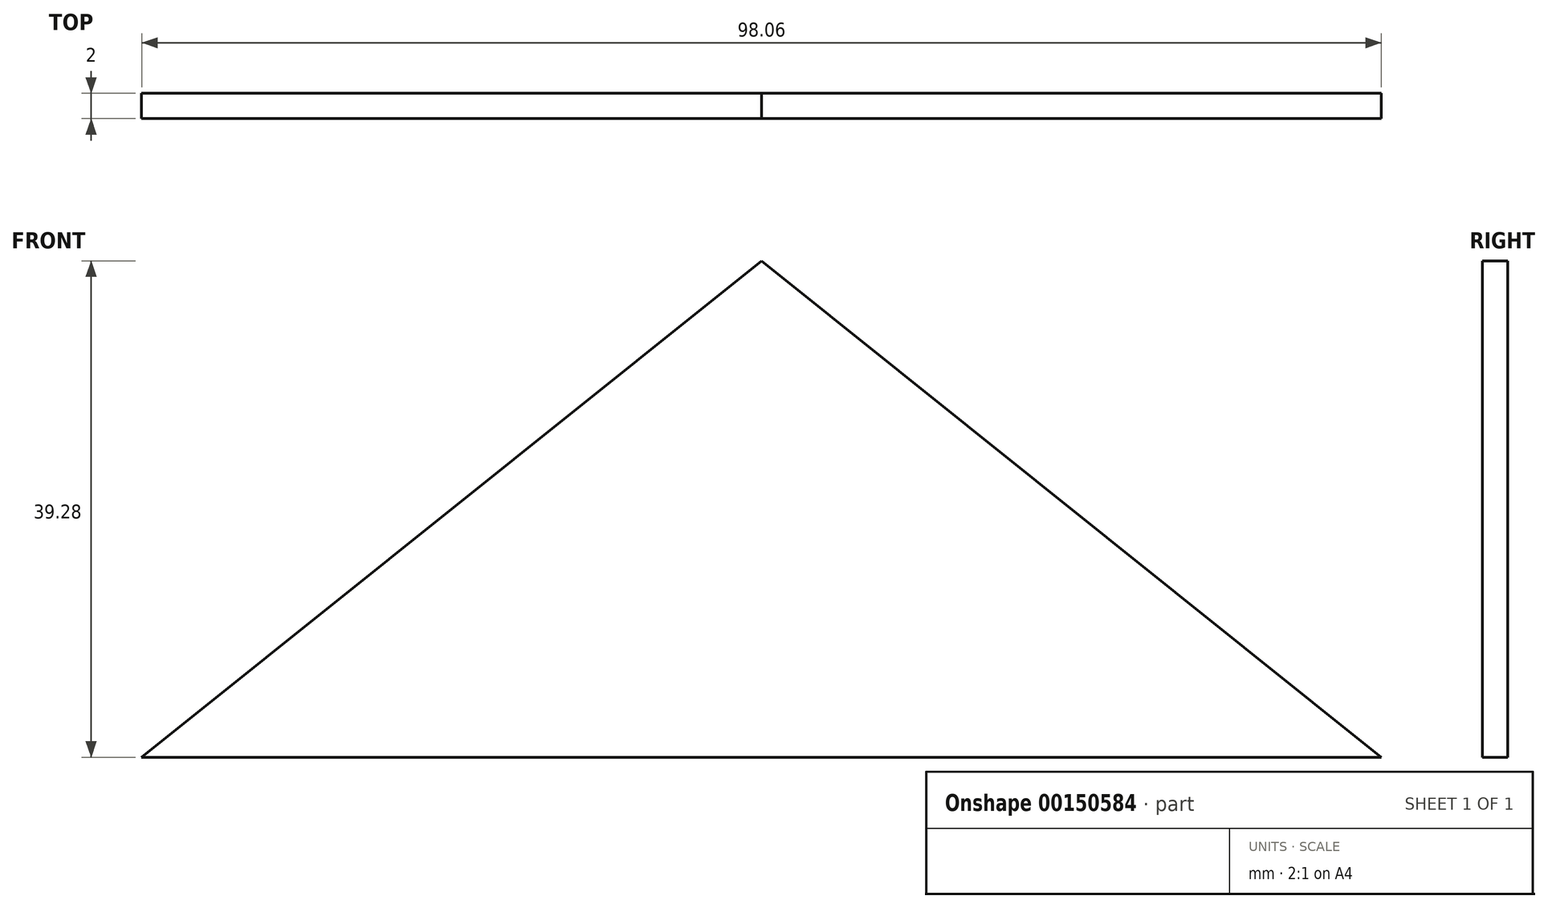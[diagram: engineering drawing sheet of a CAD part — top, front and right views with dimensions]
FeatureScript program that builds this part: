
annotation { "Feature Type Name" : "Feature", "Feature Type Description" : "" }
export const myFeature = defineFeature(function(context is Context, id is Id, definition is map)
    precondition{}
    {
        {
            var Q0;
            Q0=qCreatedBy(makeId("Front.planeOp"),FACE);
            var sketch = newSketch(context, id + "F0", { "sketchPlane" : qUnion([Q0])});
            skLineSegment(sketch, "E0", {"start": v(0, 39.28) * mm, "end": v(49.03, 0) * mm});
            skLineSegment(sketch, "E1.MirrorCS", {"start": v(0, 39.28) * mm, "end": v(-49.03, 0) * mm});
            skLineSegment(sketch, "E2", {"start": v(-49.03, 0) * mm, "end": v(49.03, 0) * mm});
            skSolve(sketch);
        }
        {
            var Q0;
            Q0 = qSketchRegion(id + "F0", true);
            extrude(context, id + "F1", {"entities" : qUnion([Q0]), "depth" : 2 * mm});
        }
    });
